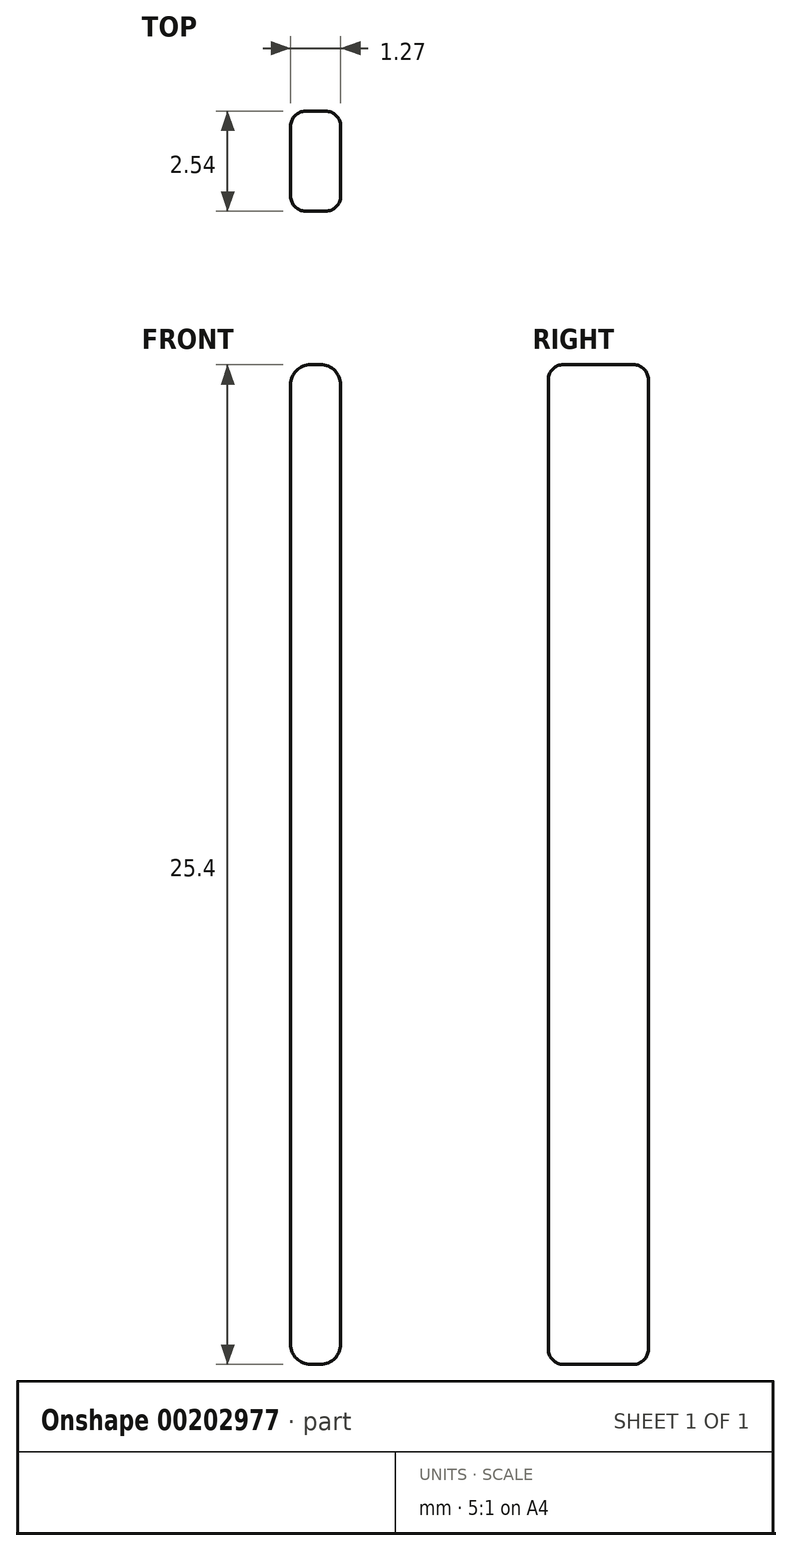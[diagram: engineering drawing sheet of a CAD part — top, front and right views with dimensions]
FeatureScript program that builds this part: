
annotation { "Feature Type Name" : "Feature", "Feature Type Description" : "" }
export const myFeature = defineFeature(function(context is Context, id is Id, definition is map)
    precondition{}
    {
        {
            var Q0;
            Q0=qCreatedBy(makeId("Front.planeOp"),FACE);
            var sketch = newSketch(context, id + "F0", { "sketchPlane" : qUnion([Q0])});
            skLineSegment(sketch, "E0.bottom", {"start": v(0, 0) * mm, "end": v(1.27, 0) * mm});
            skLineSegment(sketch, "E0.top", {"start": v(0, -25.4) * mm, "end": v(1.27, -25.4) * mm});
            skLineSegment(sketch, "E0.left", {"start": v(0, 0) * mm, "end": v(0, -25.4) * mm});
            skLineSegment(sketch, "E0.right", {"start": v(1.27, 0) * mm, "end": v(1.27, -25.4) * mm});
            skSolve(sketch);
        }
        {
            var Q0;
            Q0=makeQuery(id+"F0.imprint","IMPRINT",FACE,{"disambiguationData":[TD([[makeQuery(id+"F0.imprint","IMPRINT",EDGE,{"derivedFrom":sQuery(id+"F0.wireOp",EDGE,"E0.bottom")}),-1.0]])]});
            extrude(context, id + "F2", {"entities" : qUnion([Q0]), "depth" : 2.54 * mm});
        }
        {
            var Q0;
            Q0=makeQuery(id+"F2.opExtrude","CAP_FACE",FACE,{"disambiguationData":[OSD([sQuery(id+"F0.wireOp",EDGE,"E0.bottom"),sQuery(id+"F0.wireOp",EDGE,"E0.top"),sQuery(id+"F0.wireOp",EDGE,"E0.left"),sQuery(id+"F0.wireOp",EDGE,"E0.right")])],"isStart":false});
            var Q1;
            Q1=makeQuery(id+"F2.opExtrude","CAP_EDGE",EDGE,{"disambiguationData":[OSD([sQuery(id+"F0.wireOp",EDGE,"E0.right")])],"isStart":true});
            var Q2;
            Q2=makeQuery(id+"F2.opExtrude","CAP_FACE",FACE,{"disambiguationData":[OSD([sQuery(id+"F0.wireOp",EDGE,"E0.bottom"),sQuery(id+"F0.wireOp",EDGE,"E0.top"),sQuery(id+"F0.wireOp",EDGE,"E0.left"),sQuery(id+"F0.wireOp",EDGE,"E0.right")])],"isStart":true});
            fillet(context, id + "F3", {"entities" : qUnion([Q0, Q1, Q2]), "radius" : 0.38 * mm, "tangentPropagation" : true, "allowEdgeOverflow" : false});
        }
        {
            var Q0;
            Q0=makeQuery(id+"F2.opExtrude","SWEPT_EDGE",EDGE,{"disambiguationData":[OSD([sQuery(id+"F0.wireOp",EDGE,"E0.top"),sQuery(id+"F0.wireOp",EDGE,"E0.left")])]});
            var Q1;
            Q1=makeQuery(id+"F2.opExtrude","SWEPT_EDGE",EDGE,{"disambiguationData":[OSD([sQuery(id+"F0.wireOp",EDGE,"E0.top"),sQuery(id+"F0.wireOp",EDGE,"E0.right")])]});
            var Q2;
            Q2=makeQuery(id+"F2.opExtrude","SWEPT_EDGE",EDGE,{"disambiguationData":[OSD([sQuery(id+"F0.wireOp",EDGE,"E0.bottom"),sQuery(id+"F0.wireOp",EDGE,"E0.left")])]});
            var Q3;
            Q3=makeQuery(id+"F2.opExtrude","SWEPT_EDGE",EDGE,{"disambiguationData":[OSD([sQuery(id+"F0.wireOp",EDGE,"E0.bottom"),sQuery(id+"F0.wireOp",EDGE,"E0.right")])]});
            fillet(context, id + "F1", {"entities" : qUnion([Q0, Q1, Q2, Q3]), "radius" : 0.5 * mm, "tangentPropagation" : true, "allowEdgeOverflow" : false});
        }
    });
